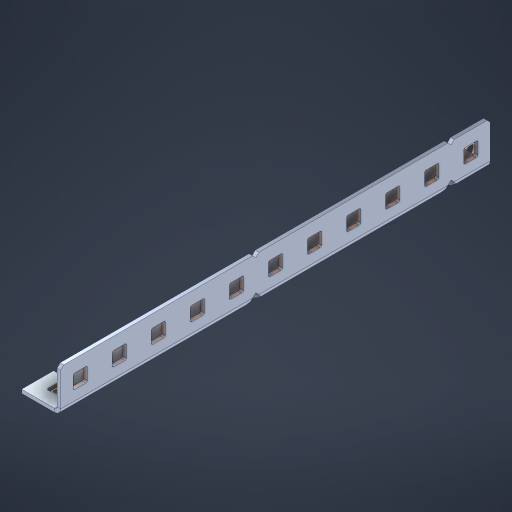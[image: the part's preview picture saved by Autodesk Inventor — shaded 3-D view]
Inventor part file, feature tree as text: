
AUTODESK INVENTOR PART (.ipt)
format: ipt  version: 2023 (Build 270158000, 158)  size: 704,000 bytes
history: native  units: in
note: dims shown in document units (in); Inventor stores cm internally (conversion verified against a paired STEP export)
features: other x40, extrude x31, sheet_metal_op x11, sketch x10, pattern_linear x2, mirror x1, chamfer x1
ambient origin geometry x8: Origin, YZ Plane, XZ Plane, XY Plane, X Axis, Y Axis, Z Axis, Center Point
bodies: Solid1 (feature_tree), Body (feature_tree)
feature tree (96):
  sheet_metal_op  "Flanges"
  other  "Flange Pattern Plane"
  other  "Flange Pattern Sketch"
  sheet_metal_op  "Flange Pattern"
  sheet_metal_op  "Body Pattern"
  pattern_linear  "Center Pattern"  Spacing1=0.0469in  [1 undecoded]
  other  "Arc Length"
  mirror  "Notch Mirror"
  pattern_linear  "Notch Pattern"  Spacing1=0.182in  [1 undecoded]
  chamfer  "End Chamfer"
  extrude  "Half Cut"  Depth=0.02in
  sketch  "Sketch1"  dims[d0=1.0in]
  other  "Plate1"
  sketch  "Sketch2"  dims[d1=5.5in]
  other  "Plate2"
  sheet_metal_op  "Bend1"
  sheet_metal_op  "Corner1"
  sketch  "Sketch3"  dims[d2=0.0469in]
  sketch  "Sketch7"  dims[d3=0.0469in]
  other  "Srf1"
  other  "Srf2"
  sketch  "Sketch8"  dims[d4=0.0234in]
  sketch  "Sketch9"  dims[d5=0.0938in]
  other  "Srf91"
  sheet_metal_op  "Body Pattern Sketch"
  other  "Srf92"
  sketch  "Sketch13"  dims[d6=0.0469in]
  sketch  "Sketch14"  dims[d7=0.5in d8=90.0deg d9=0.0312in]
  sketch  "Sketch15"  dims[d10=0.1875in]
  sketch  "Sketch16"  dims[d11=0.0469in d12=0.0469in d16=0.182in d17=0.02in d18=0.0469in d19=0.0in d20=0.25in d21=0.25in d38=4.3307in d40=0.5in d41=0.3937in d43=1.0in d46=0.172in d47=1.0in d48=0.0in d49=0.182in d50=0.02in d51=0.25in d52=0.25in d53=0.0469in d54=0.0in d55=0.172in d56=1.0in d57=0.0in d58=0.25in d60=4.3307in d62=0.5in d63=0.3937in d65=0.5in d85=0.1227in d86=0.1659in d88=0.04in d89=0.0469in d90=0.0in d91=0.04in d92=0.0491in d95=2.5in d96=0.04in d97=0.25in d98=45.0deg d99=0.25in d100=0.5in d101=0.0in d102=2.497in d106=0.182in d107=0.02in d108=0.5in d109=0.5in d110=0.0469in d111=0.0in d112=0.172in d113=0.5in d114=0.0in d117=0.5in d118=0.5in d119=0.5in]
  other  "Srf786"
  other  "Srf823"
  other  "Srf824"
  other  "Srf825"
  other  "Srf826"
  other  "Srf827"
  other  "Srf828"
  other  "Srf829"
  other  "Srf856"
  other  "Srf857"
  other  "Srf858"
  other  "Srf859"
  other  "Srf860"
  other  "Srf861"
  other  "Srf862"
  other  "Srf889"
  other  "Srf890"
  other  "Srf891"
  other  "Srf892"
  other  "Srf893"
  other  "Srf894"
  other  "Srf895"
  other  "Srf896"
  other  "Srf922"
  other  "Srf923"
  other  "Srf959"
  other  "Srf960"
  other  "Srf996"
  other  "Srf997"
  sheet_metal_op  "Flange Stamp"
  sheet_metal_op  "Flange Circle"
  sheet_metal_op  "Body Stamp"
  sheet_metal_op  "Body Circle"
  other  "Center Stamp"
  other  "Center Circle"
  sheet_metal_op  "Notch"
  extrude  "ExtrusionSrf2"  Depth=0.0469in
  extrude  "ExtrusionSrf92"  TaperAngle=0.0deg  [1 undecoded]
  extrude  "ExtrusionSrf823"  Depth=0.5in
  extrude  "ExtrusionSrf824"  Depth=0.5in
  extrude  "ExtrusionSrf825"  Depth=0.5in
  extrude  "ExtrusionSrf826"  Depth=0.5in
  extrude  "ExtrusionSrf827"  Depth=1.0in TaperAngle=0.0deg
  extrude  "ExtrusionSrf828"  Depth=0.182in
  extrude  "ExtrusionSrf829"  Depth=0.02in
  extrude  "ExtrusionSrf856"  Depth=0.5in
  extrude  "ExtrusionSrf857"  Depth=0.5in
  extrude  "ExtrusionSrf858"  Depth=0.0469in
  extrude  "ExtrusionSrf859"  TaperAngle=0.0deg  [1 undecoded]
  extrude  "ExtrusionSrf860"  Depth=0.5in
  extrude  "ExtrusionSrf861"  Depth=1.0in TaperAngle=0.0deg
  extrude  "ExtrusionSrf862"  Depth=0.5in
  extrude  "ExtrusionSrf889"  Depth=0.5in
  extrude  "ExtrusionSrf890"  Depth=0.5in
  extrude  "ExtrusionSrf891"  Depth=0.5in
  extrude  "ExtrusionSrf892"  Depth=0.5in
  extrude  "ExtrusionSrf893"  Depth=0.5in
  extrude  "ExtrusionSrf894"  Depth=0.0469in
  extrude  "ExtrusionSrf895"  TaperAngle=0.0deg  [1 undecoded]
  extrude  "ExtrusionSrf896"  Depth=0.5in
  extrude  "ExtrusionSrf922"  Depth=0.5in
  extrude  "ExtrusionSrf923"  Depth=2.5in
  extrude  "ExtrusionSrf959"  Depth=0.5in TaperAngle=45.0deg
  extrude  "ExtrusionSrf960"  Depth=0.5in
  extrude  "ExtrusionSrf996"  Depth=0.5in TaperAngle=0.0deg
  extrude  "ExtrusionSrf997"  Depth=0.5in
note: 5 required parameter values undecoded (feature->parameter linkage not recoverable at this tier; creation-order binding heuristic only, values carry confidence <= 0.55)
